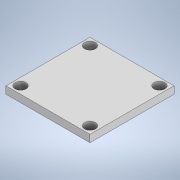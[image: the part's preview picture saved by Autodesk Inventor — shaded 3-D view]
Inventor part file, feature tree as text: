
AUTODESK INVENTOR PART (.ipt)
format: ipt  version: 2022 (Build 260153000, 153)  size: 103,936 bytes
history: native  units: mm
features: extrude x1, sketch x1
ambient origin geometry x8: Origin, YZ Plane, XZ Plane, XY Plane, X Axis, Y Axis, Z Axis, Center Point
bodies: Solid1 (feature_tree)
feature tree (2):
  extrude  "Extrusion1"  Depth=23.0mm
  sketch  "Sketch1"  dims[d0=23.0mm d1=23.0mm d4=3.0mm d5=2.0mm d6=0.0mm]
